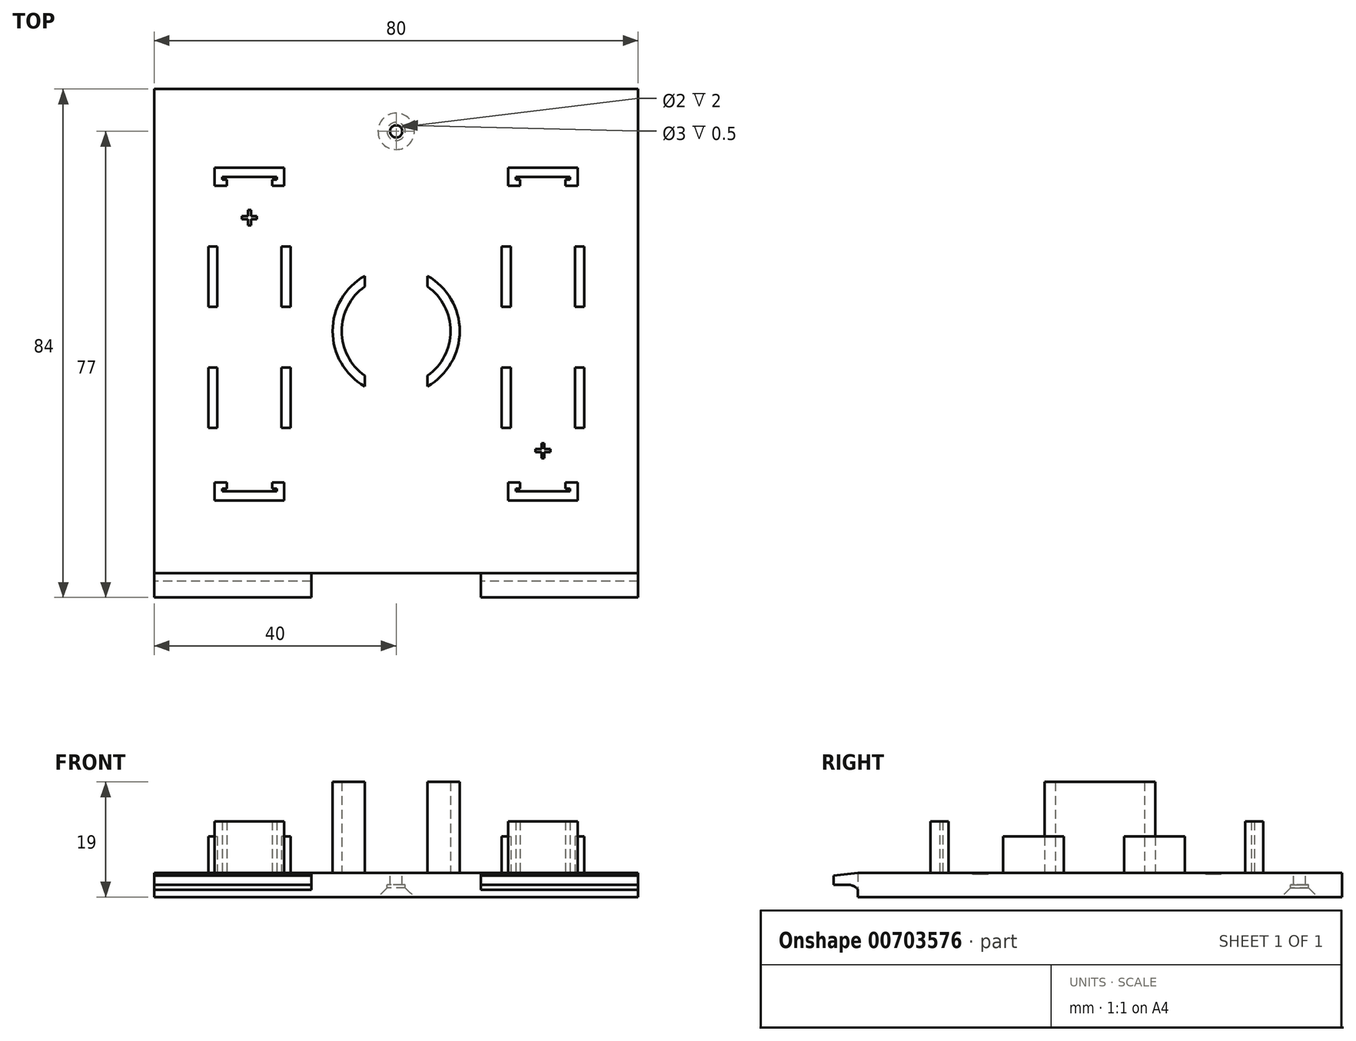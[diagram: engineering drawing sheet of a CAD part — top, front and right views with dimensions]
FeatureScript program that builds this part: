
annotation { "Feature Type Name" : "Feature", "Feature Type Description" : "" }
export const myFeature = defineFeature(function(context is Context, id is Id, definition is map)
    precondition{}
    {
        {
            var Q0;
            Q0=qCreatedBy(makeId("Top.planeOp"),FACE);
            var sketch = newSketch(context, id + "F0", { "sketchPlane" : qUnion([Q0])});
            skLineSegment(sketch, "E0.bottom", {"start": v(-40, 40) * mm, "end": v(40, 40) * mm});
            skLineSegment(sketch, "E0.top", {"start": v(-40, -40) * mm, "end": v(40, -40) * mm});
            skLineSegment(sketch, "E0.left", {"start": v(-40, 40) * mm, "end": v(-40, -40) * mm});
            skLineSegment(sketch, "E0.right", {"start": v(40, 40) * mm, "end": v(40, -40) * mm});
            skLineSegment(sketch, "E1.bottom", {"start": v(-40, -40) * mm, "end": v(-20, -40) * mm});
            skLineSegment(sketch, "E1.top", {"start": v(-40, -44) * mm, "end": v(-20, -44) * mm});
            skLineSegment(sketch, "E1.left", {"start": v(-40, -40) * mm, "end": v(-40, -44) * mm});
            skLineSegment(sketch, "E1.right", {"start": v(-20, -40) * mm, "end": v(-20, -44) * mm});
            skLineSegment(sketch, "E2.bottom", {"start": v(20, -40) * mm, "end": v(40, -40) * mm});
            skLineSegment(sketch, "E2.top", {"start": v(20, -44) * mm, "end": v(40, -44) * mm});
            skLineSegment(sketch, "E2.left", {"start": v(20, -40) * mm, "end": v(20, -44) * mm});
            skLineSegment(sketch, "E2.right", {"start": v(40, -40) * mm, "end": v(40, -44) * mm});
            skLineSegment(sketch, "E3", {"start": v(-20, -44) * mm, "end": v(20, -44) * mm});
            skLineSegment(sketch, "E4", {"start": v(-20, -40) * mm, "end": v(20, -40) * mm});
            skLineSegment(sketch, "E5", {"start": v(-14, -44) * mm, "end": v(-14, -40) * mm});
            skLineSegment(sketch, "E6", {"start": v(14, -44) * mm, "end": v(14, -40) * mm});
            skPoint(sketch, "E6.endSnap0", {"position": v(0, -40) * mm});
            skSolve(sketch);
        }
        {
            var Q0;
            Q0=makeQuery(id+"F0.imprint","IMPRINT",FACE,{"disambiguationData":[TD([[makeQuery(id+"F0.imprint","IMPRINT",EDGE,{"derivedFrom":sQuery(id+"F0.wireOp",EDGE,"E0.bottom")}),-1.0]])]});
            extrude(context, id + "F1", {"entities" : qUnion([Q0]), "depth" : 4 * mm, "offsetDistance" : 25 * mm});
        }
        {
            var Q0;
            Q0=makeQuery(id+"F1.opExtrude","CAP_FACE",FACE,{"disambiguationData":[OSD([sQuery(id+"F0.wireOp",EDGE,"E0.bottom"),sQuery(id+"F0.wireOp",EDGE,"E0.top"),sQuery(id+"F0.wireOp",EDGE,"E0.left"),sQuery(id+"F0.wireOp",EDGE,"E0.right")])],"isStart":false});
            var sketch = newSketch(context, id + "F2", { "sketchPlane" : qUnion([Q0])});
            skLineSegment(sketch, "E7.bottom", {"start": v(-30, 27) * mm, "end": v(-28, 27) * mm});
            skLineSegment(sketch, "E7.top", {"start": v(-30, 24) * mm, "end": v(-28, 24) * mm});
            skLineSegment(sketch, "E7.left", {"start": v(-30, 27) * mm, "end": v(-30, 24) * mm});
            skLineSegment(sketch, "E7.right", {"start": v(-28, 27) * mm, "end": v(-28, 24) * mm});
            skLineSegment(sketch, "E8.bottom", {"start": v(-20.5, 27) * mm, "end": v(-18.5, 27) * mm});
            skLineSegment(sketch, "E8.top", {"start": v(-20.5, 24) * mm, "end": v(-18.5, 24) * mm});
            skLineSegment(sketch, "E8.left", {"start": v(-20.5, 27) * mm, "end": v(-20.5, 24) * mm});
            skLineSegment(sketch, "E8.right", {"start": v(-18.5, 27) * mm, "end": v(-18.5, 24) * mm});
            skLineSegment(sketch, "E9", {"start": v(-28, 27) * mm, "end": v(-20.5, 27) * mm});
            skLineSegment(sketch, "E10", {"start": v(-28, 25) * mm, "end": v(-20.5, 25) * mm, "construction": true});
            skLineSegment(sketch, "E11", {"start": v(-28, 25.5) * mm, "end": v(-20.5, 25.5) * mm});
            skLineSegment(sketch, "E12", {"start": v(-28, 25.5) * mm, "end": v(-28.75, 25.5) * mm});
            skLineSegment(sketch, "E13", {"start": v(-28.75, 25.5) * mm, "end": v(-28.75, 25) * mm});
            skLineSegment(sketch, "E14", {"start": v(-28.75, 25) * mm, "end": v(-28, 25) * mm});
            skLineSegment(sketch, "E15", {"start": v(-20.5, 25.5) * mm, "end": v(-19.75, 25.5) * mm});
            skLineSegment(sketch, "E16", {"start": v(-19.75, 25.5) * mm, "end": v(-19.75, 25) * mm});
            skLineSegment(sketch, "E17", {"start": v(-19.75, 25) * mm, "end": v(-20.5, 25) * mm});
            skLineSegment(sketch, "E18.bottom", {"start": v(-18.5, -28) * mm, "end": v(-20.5, -28) * mm});
            skLineSegment(sketch, "E18.top", {"start": v(-18.5, -25) * mm, "end": v(-20.5, -25) * mm});
            skLineSegment(sketch, "E18.left", {"start": v(-18.5, -28) * mm, "end": v(-18.5, -25) * mm});
            skLineSegment(sketch, "E18.right", {"start": v(-20.5, -28) * mm, "end": v(-20.5, -25) * mm});
            skLineSegment(sketch, "E19.bottom", {"start": v(-28, -28) * mm, "end": v(-30, -28) * mm});
            skLineSegment(sketch, "E19.top", {"start": v(-28, -25) * mm, "end": v(-30, -25) * mm});
            skLineSegment(sketch, "E19.left", {"start": v(-28, -28) * mm, "end": v(-28, -25) * mm});
            skLineSegment(sketch, "E19.right", {"start": v(-30, -28) * mm, "end": v(-30, -25) * mm});
            skLineSegment(sketch, "E20", {"start": v(-20.5, -28) * mm, "end": v(-28, -28) * mm});
            skLineSegment(sketch, "E21", {"start": v(-20.5, -26) * mm, "end": v(-28, -26) * mm, "construction": true});
            skLineSegment(sketch, "E22", {"start": v(-20.5, -26.5) * mm, "end": v(-28, -26.5) * mm});
            skLineSegment(sketch, "E23", {"start": v(-20.5, -26.5) * mm, "end": v(-19.75, -26.5) * mm});
            skLineSegment(sketch, "E24", {"start": v(-19.75, -26.5) * mm, "end": v(-19.75, -26) * mm});
            skLineSegment(sketch, "E25", {"start": v(-19.75, -26) * mm, "end": v(-20.5, -26) * mm});
            skLineSegment(sketch, "E26", {"start": v(-28, -26.5) * mm, "end": v(-28.75, -26.5) * mm});
            skLineSegment(sketch, "E27", {"start": v(-28.75, -26.5) * mm, "end": v(-28.75, -26) * mm});
            skLineSegment(sketch, "E28", {"start": v(-28.75, -26) * mm, "end": v(-28, -26) * mm});
            skLineSegment(sketch, "E29.bottom", {"start": v(18.5, 27) * mm, "end": v(20.5, 27) * mm});
            skLineSegment(sketch, "E29.top", {"start": v(18.5, 24) * mm, "end": v(20.5, 24) * mm});
            skLineSegment(sketch, "E29.left", {"start": v(18.5, 27) * mm, "end": v(18.5, 24) * mm});
            skLineSegment(sketch, "E29.right", {"start": v(20.5, 27) * mm, "end": v(20.5, 24) * mm});
            skLineSegment(sketch, "E30.bottom", {"start": v(28, 27) * mm, "end": v(30, 27) * mm});
            skLineSegment(sketch, "E30.top", {"start": v(28, 24) * mm, "end": v(30, 24) * mm});
            skLineSegment(sketch, "E30.left", {"start": v(28, 27) * mm, "end": v(28, 24) * mm});
            skLineSegment(sketch, "E30.right", {"start": v(30, 27) * mm, "end": v(30, 24) * mm});
            skLineSegment(sketch, "E31", {"start": v(20.5, 27) * mm, "end": v(28, 27) * mm});
            skLineSegment(sketch, "E32", {"start": v(20.5, 25) * mm, "end": v(28, 25) * mm, "construction": true});
            skLineSegment(sketch, "E33", {"start": v(20.5, 25.5) * mm, "end": v(28, 25.5) * mm});
            skLineSegment(sketch, "E34", {"start": v(20.5, 25.5) * mm, "end": v(19.75, 25.5) * mm});
            skLineSegment(sketch, "E35", {"start": v(19.75, 25.5) * mm, "end": v(19.75, 25) * mm});
            skLineSegment(sketch, "E36", {"start": v(19.75, 25) * mm, "end": v(20.5, 25) * mm});
            skLineSegment(sketch, "E37", {"start": v(28, 25.5) * mm, "end": v(28.75, 25.5) * mm});
            skLineSegment(sketch, "E38", {"start": v(28.75, 25.5) * mm, "end": v(28.75, 25) * mm});
            skLineSegment(sketch, "E39", {"start": v(28.75, 25) * mm, "end": v(28, 25) * mm});
            skLineSegment(sketch, "E40.bottom", {"start": v(30, -28) * mm, "end": v(28, -28) * mm});
            skLineSegment(sketch, "E40.top", {"start": v(30, -25) * mm, "end": v(28, -25) * mm});
            skLineSegment(sketch, "E40.left", {"start": v(30, -28) * mm, "end": v(30, -25) * mm});
            skLineSegment(sketch, "E40.right", {"start": v(28, -28) * mm, "end": v(28, -25) * mm});
            skLineSegment(sketch, "E41.bottom", {"start": v(20.5, -28) * mm, "end": v(18.5, -28) * mm});
            skLineSegment(sketch, "E41.top", {"start": v(20.5, -25) * mm, "end": v(18.5, -25) * mm});
            skLineSegment(sketch, "E41.left", {"start": v(20.5, -28) * mm, "end": v(20.5, -25) * mm});
            skLineSegment(sketch, "E41.right", {"start": v(18.5, -28) * mm, "end": v(18.5, -25) * mm});
            skLineSegment(sketch, "E42", {"start": v(28, -28) * mm, "end": v(20.5, -28) * mm});
            skLineSegment(sketch, "E43", {"start": v(28, -26) * mm, "end": v(20.5, -26) * mm, "construction": true});
            skLineSegment(sketch, "E44", {"start": v(28, -26.5) * mm, "end": v(20.5, -26.5) * mm});
            skLineSegment(sketch, "E45", {"start": v(28, -26.5) * mm, "end": v(28.75, -26.5) * mm});
            skLineSegment(sketch, "E46", {"start": v(28.75, -26.5) * mm, "end": v(28.75, -26) * mm});
            skLineSegment(sketch, "E47", {"start": v(28.75, -26) * mm, "end": v(28, -26) * mm});
            skLineSegment(sketch, "E48", {"start": v(20.5, -26.5) * mm, "end": v(19.75, -26.5) * mm});
            skLineSegment(sketch, "E49", {"start": v(19.75, -26.5) * mm, "end": v(19.75, -26) * mm});
            skLineSegment(sketch, "E50", {"start": v(19.75, -26) * mm, "end": v(20.5, -26) * mm});
            skLineSegment(sketch, "E51", {"start": v(-18.5, 27) * mm, "end": v(18.5, 27) * mm, "construction": true});
            skLineSegment(sketch, "E52", {"start": v(-24.25, 25) * mm, "end": v(-24.25, -26) * mm, "construction": true});
            skLineSegment(sketch, "E53", {"start": v(24.25, 25) * mm, "end": v(24.25, -26) * mm, "construction": true});
            skLineSegment(sketch, "E54.bottom", {"start": v(-31.05, 14) * mm, "end": v(-29.55, 14) * mm});
            skLineSegment(sketch, "E54.top", {"start": v(-31.05, 4) * mm, "end": v(-29.55, 4) * mm});
            skLineSegment(sketch, "E54.left", {"start": v(-31.05, 14) * mm, "end": v(-31.05, 4) * mm});
            skLineSegment(sketch, "E54.right", {"start": v(-29.55, 14) * mm, "end": v(-29.55, 4) * mm});
            skLineSegment(sketch, "E55", {"start": v(-30, 24) * mm, "end": v(-42.81, 24) * mm, "construction": true});
            skLineSegment(sketch, "E56.bottom", {"start": v(-31.05, -6) * mm, "end": v(-29.55, -6) * mm});
            skLineSegment(sketch, "E56.top", {"start": v(-31.05, -16) * mm, "end": v(-29.55, -16) * mm});
            skLineSegment(sketch, "E56.left", {"start": v(-31.05, -6) * mm, "end": v(-31.05, -16) * mm});
            skLineSegment(sketch, "E56.right", {"start": v(-29.55, -6) * mm, "end": v(-29.55, -16) * mm});
            skLineSegment(sketch, "E57.MirrorCS", {"start": v(-18.95, 14) * mm, "end": v(-18.95, 4) * mm});
            skLineSegment(sketch, "E58.MirrorCS", {"start": v(-17.45, 14) * mm, "end": v(-17.45, 4) * mm});
            skLineSegment(sketch, "E59.MirrorCS", {"start": v(-17.45, 14) * mm, "end": v(-18.95, 14) * mm});
            skLineSegment(sketch, "E60.MirrorCS", {"start": v(-17.45, 4) * mm, "end": v(-18.95, 4) * mm});
            skLineSegment(sketch, "E61.MirrorCS", {"start": v(-18.95, -6) * mm, "end": v(-18.95, -16) * mm});
            skLineSegment(sketch, "E62.MirrorCS", {"start": v(-17.45, -6) * mm, "end": v(-17.45, -16) * mm});
            skLineSegment(sketch, "E63.MirrorCS", {"start": v(-17.45, -6) * mm, "end": v(-18.95, -6) * mm});
            skLineSegment(sketch, "E64.MirrorCS", {"start": v(-17.45, -16) * mm, "end": v(-18.95, -16) * mm});
            skLineSegment(sketch, "E65", {"start": v(18.5, 24) * mm, "end": v(3.37, 24) * mm, "construction": true});
            skLineSegment(sketch, "E66.bottom", {"start": v(17.45, 14) * mm, "end": v(18.95, 14) * mm});
            skLineSegment(sketch, "E66.top", {"start": v(17.45, 4) * mm, "end": v(18.95, 4) * mm});
            skLineSegment(sketch, "E66.left", {"start": v(17.45, 14) * mm, "end": v(17.45, 4) * mm});
            skLineSegment(sketch, "E66.right", {"start": v(18.95, 14) * mm, "end": v(18.95, 4) * mm});
            skLineSegment(sketch, "E67.bottom", {"start": v(17.45, -6) * mm, "end": v(18.95, -6) * mm});
            skLineSegment(sketch, "E67.top", {"start": v(17.45, -16) * mm, "end": v(18.95, -16) * mm});
            skLineSegment(sketch, "E67.left", {"start": v(17.45, -6) * mm, "end": v(17.45, -16) * mm});
            skLineSegment(sketch, "E67.right", {"start": v(18.95, -6) * mm, "end": v(18.95, -16) * mm});
            skLineSegment(sketch, "E68.MirrorCS", {"start": v(29.55, 14) * mm, "end": v(29.55, 4) * mm});
            skLineSegment(sketch, "E69.MirrorCS", {"start": v(31.05, 14) * mm, "end": v(31.05, 4) * mm});
            skLineSegment(sketch, "E70.MirrorCS", {"start": v(31.05, 4) * mm, "end": v(29.55, 4) * mm});
            skLineSegment(sketch, "E71.MirrorCS", {"start": v(31.05, 14) * mm, "end": v(29.55, 14) * mm});
            skLineSegment(sketch, "E72.MirrorCS", {"start": v(31.05, -6) * mm, "end": v(29.55, -6) * mm});
            skLineSegment(sketch, "E73.MirrorCS", {"start": v(29.55, -6) * mm, "end": v(29.55, -16) * mm});
            skLineSegment(sketch, "E74.MirrorCS", {"start": v(31.05, -6) * mm, "end": v(31.05, -16) * mm});
            skLineSegment(sketch, "E75.MirrorCS", {"start": v(31.05, -16) * mm, "end": v(29.55, -16) * mm});
            skLineSegment(sketch, "E76", {"start": v(-28, -25) * mm, "end": v(-20.5, -25) * mm, "construction": true});
            skLineSegment(sketch, "E77", {"start": v(20.5, -25) * mm, "end": v(28, -25) * mm, "construction": true});
            skLineSegment(sketch, "E78", {"start": v(20.5, 24) * mm, "end": v(28, 24) * mm, "construction": true});
            skLineSegment(sketch, "E79", {"start": v(-28, 24) * mm, "end": v(-20.5, 24) * mm, "construction": true});
            skLineSegment(sketch, "E80.bottom", {"start": v(-24.5, 20) * mm, "end": v(-24, 20) * mm});
            skLineSegment(sketch, "E80.top", {"start": v(-24.5, 17.5) * mm, "end": v(-24, 17.5) * mm});
            skLineSegment(sketch, "E80.left", {"start": v(-24.5, 20) * mm, "end": v(-24.5, 19) * mm});
            skLineSegment(sketch, "E80.right", {"start": v(-24, 20) * mm, "end": v(-24, 19) * mm});
            skLineSegment(sketch, "E81.bottom", {"start": v(-23, 19) * mm, "end": v(-24, 19) * mm});
            skLineSegment(sketch, "E81.top", {"start": v(-23, 18.5) * mm, "end": v(-24, 18.5) * mm});
            skLineSegment(sketch, "E81.left", {"start": v(-23, 19) * mm, "end": v(-23, 18.5) * mm});
            skLineSegment(sketch, "E81.right", {"start": v(-25.5, 19) * mm, "end": v(-25.5, 18.5) * mm});
            skLineSegment(sketch, "E82", {"start": v(-25.5, 18.75) * mm, "end": v(-23, 18.75) * mm, "construction": true});
            skLineSegment(sketch, "E83", {"start": v(-24.25, 20) * mm, "end": v(-24.25, 17.5) * mm, "construction": true});
            skLineSegment(sketch, "E84.trimOffspring", {"start": v(-24.5, 18.5) * mm, "end": v(-24.5, 17.5) * mm});
            skLineSegment(sketch, "E85.trimOffspring", {"start": v(-24.5, 18.5) * mm, "end": v(-25.5, 18.5) * mm});
            skLineSegment(sketch, "E86.trimOffspring", {"start": v(-24, 18.5) * mm, "end": v(-24, 17.5) * mm});
            skLineSegment(sketch, "E87.trimOffspring", {"start": v(-24.5, 19) * mm, "end": v(-25.5, 19) * mm});
            skLineSegment(sketch, "E88.bottom", {"start": v(24, -18.5) * mm, "end": v(24.5, -18.5) * mm});
            skLineSegment(sketch, "E88.top", {"start": v(24, -21) * mm, "end": v(24.5, -21) * mm});
            skLineSegment(sketch, "E88.left", {"start": v(24, -18.5) * mm, "end": v(24, -19.5) * mm});
            skLineSegment(sketch, "E88.right", {"start": v(24.5, -18.5) * mm, "end": v(24.5, -19.5) * mm});
            skLineSegment(sketch, "E89.bottom", {"start": v(25.5, -19.5) * mm, "end": v(24.5, -19.5) * mm});
            skLineSegment(sketch, "E89.top", {"start": v(25.5, -20) * mm, "end": v(24.5, -20) * mm});
            skLineSegment(sketch, "E89.left", {"start": v(25.5, -19.5) * mm, "end": v(25.5, -20) * mm});
            skLineSegment(sketch, "E89.right", {"start": v(23, -19.5) * mm, "end": v(23, -20) * mm});
            skLineSegment(sketch, "E90", {"start": v(23, -19.75) * mm, "end": v(25.5, -19.75) * mm, "construction": true});
            skLineSegment(sketch, "E91", {"start": v(24.25, -18.5) * mm, "end": v(24.25, -21) * mm, "construction": true});
            skLineSegment(sketch, "E92.trimOffspring", {"start": v(24, -20) * mm, "end": v(24, -21) * mm});
            skLineSegment(sketch, "E93.trimOffspring", {"start": v(24, -20) * mm, "end": v(23, -20) * mm});
            skLineSegment(sketch, "E94.trimOffspring", {"start": v(24.5, -20) * mm, "end": v(24.5, -21) * mm});
            skLineSegment(sketch, "E95.trimOffspring", {"start": v(24, -19.5) * mm, "end": v(23, -19.5) * mm});
            skSolve(sketch);
        }
        {
            var Q0;
            Q0=makeQuery(id+"F2.imprint","IMPRINT",FACE,{"disambiguationData":[TD([[makeQuery(id+"F2.imprint","IMPRINT",EDGE,{"derivedFrom":sQuery(id+"F2.wireOp",EDGE,"E56.bottom")}),-1.0]])]});
            var Q1;
            Q1=makeQuery(id+"F2.imprint","IMPRINT",FACE,{"disambiguationData":[TD([[makeQuery(id+"F2.imprint","IMPRINT",EDGE,{"derivedFrom":sQuery(id+"F2.wireOp",EDGE,"E61.MirrorCS")}),1.0]])]});
            var Q2;
            Q2=makeQuery(id+"F2.imprint","IMPRINT",FACE,{"disambiguationData":[TD([[makeQuery(id+"F2.imprint","IMPRINT",EDGE,{"derivedFrom":sQuery(id+"F2.wireOp",EDGE,"E57.MirrorCS")}),1.0]])]});
            var Q3;
            Q3=makeQuery(id+"F2.imprint","IMPRINT",FACE,{"disambiguationData":[TD([[makeQuery(id+"F2.imprint","IMPRINT",EDGE,{"derivedFrom":sQuery(id+"F2.wireOp",EDGE,"E54.bottom")}),-1.0]])]});
            var Q4;
            Q4=makeQuery(id+"F2.imprint","IMPRINT",FACE,{"disambiguationData":[TD([[makeQuery(id+"F2.imprint","IMPRINT",EDGE,{"derivedFrom":sQuery(id+"F2.wireOp",EDGE,"E67.bottom")}),-1.0]])]});
            var Q5;
            Q5=makeQuery(id+"F2.imprint","IMPRINT",FACE,{"disambiguationData":[TD([[makeQuery(id+"F2.imprint","IMPRINT",EDGE,{"derivedFrom":sQuery(id+"F2.wireOp",EDGE,"E66.bottom")}),-1.0]])]});
            var Q6;
            Q6=makeQuery(id+"F2.imprint","IMPRINT",FACE,{"disambiguationData":[TD([[makeQuery(id+"F2.imprint","IMPRINT",EDGE,{"derivedFrom":sQuery(id+"F2.wireOp",EDGE,"E68.MirrorCS")}),1.0]])]});
            var Q7;
            Q7=makeQuery(id+"F2.imprint","IMPRINT",FACE,{"disambiguationData":[TD([[makeQuery(id+"F2.imprint","IMPRINT",EDGE,{"derivedFrom":sQuery(id+"F2.wireOp",EDGE,"E72.MirrorCS")}),1.0]])]});
            extrude(context, id + "F3", {"entities" : qUnion([Q0, Q1, Q2, Q3, Q4, Q5, Q6, Q7]), "operationType" : NewBodyOperationType.ADD, "depth" : 6 * mm, "offsetDistance" : 25 * mm});
        }
        {
            var Q0;
            {var subQ1=sQuery(id+"F2.wireOp",EDGE,"E7.bottom");Q0=makeQuery(id+"F2.imprint","IMPRINT",FACE,{"disambiguationData":[TD([[makeQuery(id+"F2.imprint","IMPRINT",EDGE,{"derivedFrom":subQ1}),-1.0]])]});}
            var Q1;
            {var subQ0=sQuery(id+"F2.wireOp",EDGE,"E9");Q1=makeQuery(id+"F2.imprint","IMPRINT",FACE,{"disambiguationData":[TD([[makeQuery(id+"F2.imprint","IMPRINT",EDGE,{"derivedFrom":subQ0}),-1.0]])]});}
            var Q2;
            {var subQ3=sQuery(id+"F2.wireOp",EDGE,"E8.bottom");Q2=makeQuery(id+"F2.imprint","IMPRINT",FACE,{"disambiguationData":[TD([[makeQuery(id+"F2.imprint","IMPRINT",EDGE,{"derivedFrom":subQ3}),-1.0]])]});}
            var Q3;
            {var subQ1=sQuery(id+"F2.wireOp",EDGE,"E18.bottom");Q3=makeQuery(id+"F2.imprint","IMPRINT",FACE,{"disambiguationData":[TD([[makeQuery(id+"F2.imprint","IMPRINT",EDGE,{"derivedFrom":subQ1}),-1.0]])]});}
            var Q4;
            {var subQ0=sQuery(id+"F2.wireOp",EDGE,"E20");Q4=makeQuery(id+"F2.imprint","IMPRINT",FACE,{"disambiguationData":[TD([[makeQuery(id+"F2.imprint","IMPRINT",EDGE,{"derivedFrom":subQ0}),-1.0]])]});}
            var Q5;
            {var subQ3=sQuery(id+"F2.wireOp",EDGE,"E19.bottom");Q5=makeQuery(id+"F2.imprint","IMPRINT",FACE,{"disambiguationData":[TD([[makeQuery(id+"F2.imprint","IMPRINT",EDGE,{"derivedFrom":subQ3}),-1.0]])]});}
            var Q6;
            {var subQ1=sQuery(id+"F2.wireOp",EDGE,"E29.bottom");Q6=makeQuery(id+"F2.imprint","IMPRINT",FACE,{"disambiguationData":[TD([[makeQuery(id+"F2.imprint","IMPRINT",EDGE,{"derivedFrom":subQ1}),-1.0]])]});}
            var Q7;
            {var subQ0=sQuery(id+"F2.wireOp",EDGE,"E31");Q7=makeQuery(id+"F2.imprint","IMPRINT",FACE,{"disambiguationData":[TD([[makeQuery(id+"F2.imprint","IMPRINT",EDGE,{"derivedFrom":subQ0}),-1.0]])]});}
            var Q8;
            {var subQ3=sQuery(id+"F2.wireOp",EDGE,"E30.bottom");Q8=makeQuery(id+"F2.imprint","IMPRINT",FACE,{"disambiguationData":[TD([[makeQuery(id+"F2.imprint","IMPRINT",EDGE,{"derivedFrom":subQ3}),-1.0]])]});}
            var Q9;
            {var subQ1=sQuery(id+"F2.wireOp",EDGE,"E40.bottom");Q9=makeQuery(id+"F2.imprint","IMPRINT",FACE,{"disambiguationData":[TD([[makeQuery(id+"F2.imprint","IMPRINT",EDGE,{"derivedFrom":subQ1}),-1.0]])]});}
            var Q10;
            {var subQ0=sQuery(id+"F2.wireOp",EDGE,"E42");Q10=makeQuery(id+"F2.imprint","IMPRINT",FACE,{"disambiguationData":[TD([[makeQuery(id+"F2.imprint","IMPRINT",EDGE,{"derivedFrom":subQ0}),-1.0]])]});}
            var Q11;
            {var subQ3=sQuery(id+"F2.wireOp",EDGE,"E41.bottom");Q11=makeQuery(id+"F2.imprint","IMPRINT",FACE,{"disambiguationData":[TD([[makeQuery(id+"F2.imprint","IMPRINT",EDGE,{"derivedFrom":subQ3}),-1.0]])]});}
            extrude(context, id + "F4", {"entities" : qUnion([Q0, Q1, Q2, Q3, Q4, Q5, Q6, Q7, Q8, Q9, Q10, Q11]), "operationType" : NewBodyOperationType.ADD, "depth" : 8.5 * mm, "offsetDistance" : 25 * mm});
        }
        {
            var Q0;
            Q0=makeQuery(id+"F1.opExtrude","CAP_FACE",FACE,{"disambiguationData":[OSD([sQuery(id+"F0.wireOp",EDGE,"E0.bottom"),sQuery(id+"F0.wireOp",EDGE,"E0.top"),sQuery(id+"F0.wireOp",EDGE,"E0.left"),sQuery(id+"F0.wireOp",EDGE,"E0.right")])],"isStart":false});
            var sketch = newSketch(context, id + "F5", { "sketchPlane" : qUnion([Q0])});
            skCircle(sketch, "E96", {"center": v(0, 33) * mm, "radius": 1.5 * mm});
            skCircle(sketch, "E97", {"center": v(0, 33) * mm, "radius": 1 * mm});
            skSolve(sketch);
        }
        {
            var Q0;
            Q0=makeQuery(id+"F5.imprint","IMPRINT",FACE,{"disambiguationData":[TD([[makeQuery(id+"F5.imprint","IMPRINT",EDGE,{"derivedFrom":sQuery(id+"F5.wireOp",EDGE,"E97")}),1.0]])]});
            extrude(context, id + "F6", {"entities" : qUnion([Q0]), "operationType" : NewBodyOperationType.REMOVE, "oppositeDirection" : true, "depth" : 25 * mm, "offsetDistance" : 25 * mm});
        }
        {
            var Q0;
            Q0=makeQuery(id+"F5.imprint","IMPRINT",FACE,{"disambiguationData":[TD([[makeQuery(id+"F5.imprint","IMPRINT",EDGE,{"derivedFrom":sQuery(id+"F5.wireOp",EDGE,"E96")}),1.0]])]});
            extrude(context, id + "F7", {"entities" : qUnion([Q0]), "operationType" : NewBodyOperationType.REMOVE, "oppositeDirection" : true, "depth" : 25 * mm, "offsetDistance" : 25 * mm, "hasSecondDirection" : true, "secondDirectionOppositeDirection" : true, "secondDirectionDepth" : 2 * mm});
        }
        {
            var Q0;
            Q0=makeQuery(id+"F7.boolean.opBoolean","INTERSECT",EDGE,{"derivedFrom":[makeQuery(id+"F1.opExtrude","CAP_FACE",FACE,{"disambiguationData":[OSD([sQuery(id+"F0.wireOp",EDGE,"E0.bottom"),sQuery(id+"F0.wireOp",EDGE,"E0.top"),sQuery(id+"F0.wireOp",EDGE,"E0.left"),sQuery(id+"F0.wireOp",EDGE,"E0.right")])],"isStart":true}),makeQuery(id+"F7.opExtrude","SWEPT_FACE",FACE,{"disambiguationData":[OSD([sQuery(id+"F5.wireOp",EDGE,"E96")])]})]});
            chamfer(context, id + "F8", {"entities" : qUnion([Q0]), "width" : 1.5 * mm, "tangentPropagation" : true});
        }
        {
            var Q0;
            Q0=qCreatedBy(makeId("Right.planeOp"),FACE);
            var sketch = newSketch(context, id + "F9", { "sketchPlane" : qUnion([Q0])});
            skLineSegment(sketch, "E98", {"start": v(-44, 2) * mm, "end": v(-40, 2) * mm});
            skLineSegment(sketch, "E99", {"start": v(-44, 4) * mm, "end": v(-40, 4) * mm});
            skLineSegment(sketch, "E100", {"start": v(-44, 4) * mm, "end": v(-44, 2) * mm});
            skLineSegment(sketch, "E101", {"start": v(-40, 2) * mm, "end": v(-40, 4) * mm});
            skLineSegment(sketch, "E102", {"start": v(-47.4, 0) * mm, "end": v(-39.16, 0) * mm});
            skLineSegment(sketch, "E103", {"start": v(-40, 2) * mm, "end": v(-40, 0) * mm});
            skFitSpline(sketch, "E104", {"points": [v(-40, 1.17) * mm, v(-40.47, 1.69) * mm, v(-41.33, 2) * mm], "startDerivative": vector(-0.67, 1.12) * mm, "endDerivative": vector(-1.92, 0.56) * mm});
            skLineSegment(sketch, "E105", {"start": v(-44, 3.5) * mm, "end": v(-40, 4) * mm});
            skSolve(sketch);
        }
        {
            var Q0;
            {var subQ4=sQuery(id+"F9.wireOp",EDGE,"E101");Q0=makeQuery(id+"F9.imprint","IMPRINT",FACE,{"disambiguationData":[TD([[makeQuery(id+"F9.imprint","IMPRINT",EDGE,{"derivedFrom":subQ4}),1.0]])]});}
            var Q1;
            {var subQ3=sQuery(id+"F9.wireOp",EDGE,"E104");Q1=makeQuery(id+"F9.imprint","IMPRINT",FACE,{"disambiguationData":[TD([[makeQuery(id+"F9.imprint","IMPRINT",EDGE,{"derivedFrom":subQ3}),-1.0]])]});}
            extrude(context, id + "F10", {"entities" : qUnion([Q0, Q1]), "operationType" : NewBodyOperationType.ADD, "depth" : 40 * mm, "offsetDistance" : 25 * mm, "hasSecondDirection" : true, "secondDirectionOppositeDirection" : true, "secondDirectionDepth" : 40 * mm});
        }
        {
            var Q0;
            Q0=makeQuery(id+"F0.imprint","IMPRINT",FACE,{"disambiguationData":[TD([[makeQuery(id+"F0.imprint","IMPRINT",EDGE,{"derivedFrom":sQuery(id+"F0.wireOp",EDGE,"E1.bottom")}),-1.0]])]});
            var Q1;
            {var subQ0=sQuery(id+"F0.wireOp",EDGE,"E5");Q1=makeQuery(id+"F0.imprint","IMPRINT",FACE,{"disambiguationData":[TD([[makeQuery(id+"F0.imprint","IMPRINT",EDGE,{"derivedFrom":subQ0}),-1.0]])]});}
            var Q2;
            Q2=makeQuery(id+"F0.imprint","IMPRINT",FACE,{"disambiguationData":[TD([[makeQuery(id+"F0.imprint","IMPRINT",EDGE,{"derivedFrom":sQuery(id+"F0.wireOp",EDGE,"E2.bottom")}),-1.0]])]});
            extrude(context, id + "F11", {"entities" : qUnion([Q0, Q1, Q2]), "operationType" : NewBodyOperationType.REMOVE, "depth" : 18.6 * mm, "offsetDistance" : 25 * mm});
        }
        {
            var Q0;
            Q0=makeQuery(id+"F2.imprint","IMPRINT",FACE,{"disambiguationData":[TD([[makeQuery(id+"F2.imprint","IMPRINT",EDGE,{"derivedFrom":sQuery(id+"F2.wireOp",EDGE,"E80.bottom")}),-1.0]])]});
            var Q1;
            Q1=makeQuery(id+"F2.imprint","IMPRINT",FACE,{"disambiguationData":[TD([[makeQuery(id+"F2.imprint","IMPRINT",EDGE,{"derivedFrom":sQuery(id+"F2.wireOp",EDGE,"E88.bottom")}),-1.0]])]});
            extrude(context, id + "F12", {"entities" : qUnion([Q0, Q1]), "operationType" : NewBodyOperationType.REMOVE, "oppositeDirection" : true, "depth" : .3 * mm, "offsetDistance" : 25 * mm});
        }
        {
            var Q0;
            Q0=makeQuery(id+"F1.opExtrude","CAP_FACE",FACE,{"disambiguationData":[OSD([sQuery(id+"F0.wireOp",EDGE,"E0.bottom"),sQuery(id+"F0.wireOp",EDGE,"E0.left"),sQuery(id+"F0.wireOp",EDGE,"E0.right"),sQuery(id+"F0.wireOp",EDGE,"E1.bottom"),sQuery(id+"F0.wireOp",EDGE,"E2.bottom"),sQuery(id+"F0.wireOp",EDGE,"E4")])],"isStart":false});
            var sketch = newSketch(context, id + "F13", { "sketchPlane" : qUnion([Q0])});
            skCircle(sketch, "E106", {"center": v(0, 0) * mm, "radius": 9 * mm});
            skCircle(sketch, "E107", {"center": v(0, 0) * mm, "radius": 10.5 * mm});
            skCircle(sketch, "E108", {"center": v(0, 0) * mm, "radius": 3 * mm});
            skLineSegment(sketch, "E109", {"start": v(-5.2, 9.12) * mm, "end": v(-5.2, -9.12) * mm});
            skLineSegment(sketch, "E110", {"start": v(5.2, 9.12) * mm, "end": v(5.2, -9.12) * mm});
            skSolve(sketch);
        }
        {
            var Q0;
            {var subQ0=sQuery(id+"F13.wireOp",EDGE,"E109");var subQ1=sQuery(id+"F13.wireOp",EDGE,"E106");var subQ2=makeQuery(id+"F13.imprint","INTERSECT",VERTEX,{"disambiguationData":[OD(0.0)],"derivedFrom":[subQ1,subQ0]});Q0=makeQuery(id+"F13.imprint","IMPRINT",FACE,{"disambiguationData":[TD([[makeQuery(id+"F13.imprint","IMPRINT",EDGE,{"disambiguationData":[TD([[subQ2,-1.0]])],"derivedFrom":subQ1}),-1.0]])]});}
            var Q1;
            {var subQ0=sQuery(id+"F13.wireOp",EDGE,"E110");var subQ1=sQuery(id+"F13.wireOp",EDGE,"E106");var subQ2=makeQuery(id+"F13.imprint","INTERSECT",VERTEX,{"disambiguationData":[OD(0.0)],"derivedFrom":[subQ1,subQ0]});Q1=makeQuery(id+"F13.imprint","IMPRINT",FACE,{"disambiguationData":[TD([[makeQuery(id+"F13.imprint","IMPRINT",EDGE,{"disambiguationData":[TD([[subQ2,1.0]])],"derivedFrom":subQ1}),-1.0]])]});}
            extrude(context, id + "F14", {"entities" : qUnion([Q0, Q1]), "operationType" : NewBodyOperationType.ADD, "depth" : 15 * mm, "offsetDistance" : 25 * mm});
        }
    });
